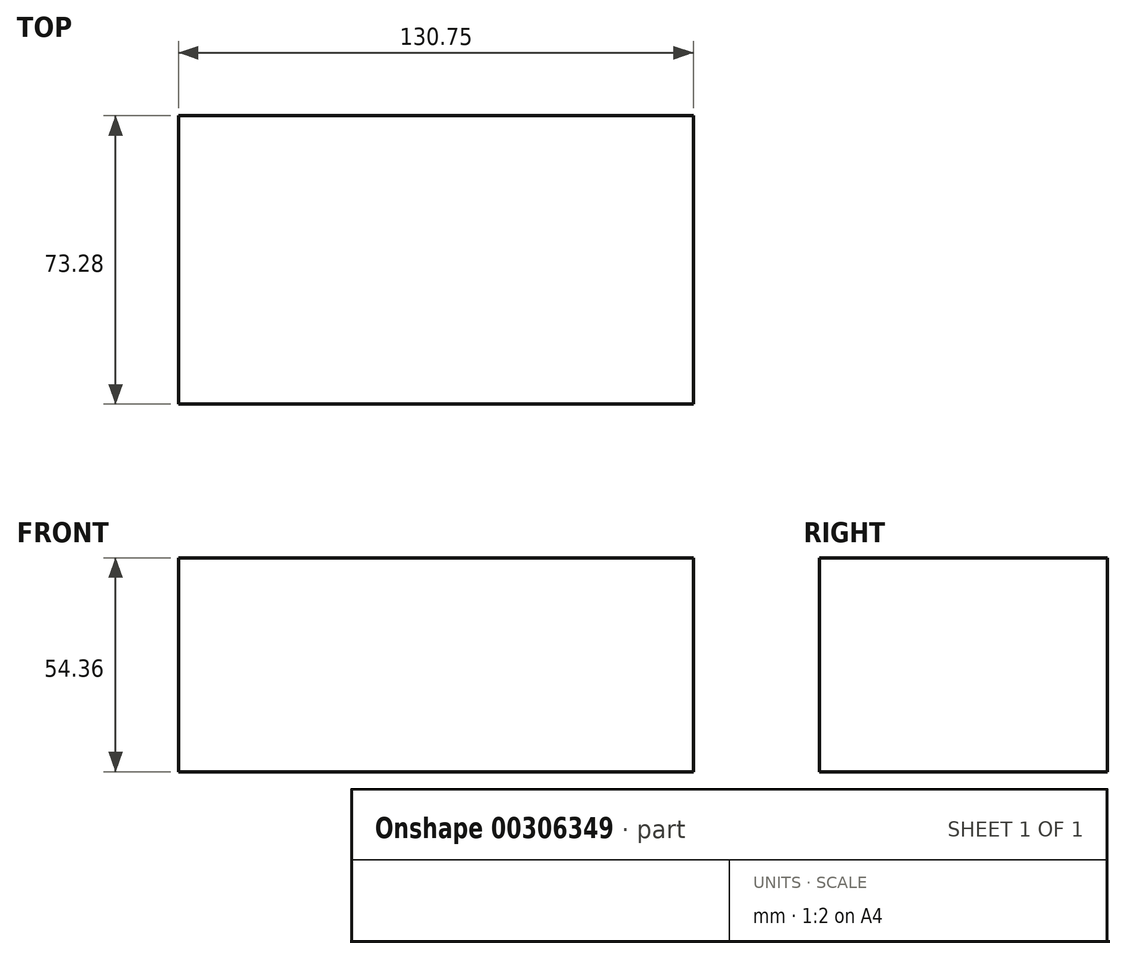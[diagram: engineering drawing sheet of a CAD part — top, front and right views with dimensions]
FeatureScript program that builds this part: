
annotation { "Feature Type Name" : "Feature", "Feature Type Description" : "" }
export const myFeature = defineFeature(function(context is Context, id is Id, definition is map)
    precondition{}
    {
        {
            var Q0;
            Q0=qCreatedBy(makeId("Top.planeOp"),FACE);
            var sketch = newSketch(context, id + "F0", { "sketchPlane" : qUnion([Q0])});
            skLineSegment(sketch, "E0.bottom", {"start": v(-61.48, 0) * mm, "end": v(69.27, 0) * mm});
            skLineSegment(sketch, "E0.top", {"start": v(-61.48, 73.28) * mm, "end": v(69.27, 73.28) * mm});
            skLineSegment(sketch, "E0.left", {"start": v(-61.48, 0) * mm, "end": v(-61.48, 73.28) * mm});
            skLineSegment(sketch, "E0.right", {"start": v(69.27, 0) * mm, "end": v(69.27, 73.28) * mm});
            skSolve(sketch);
        }
        {
            var Q0;
            Q0=makeQuery(id+"F0.imprint","IMPRINT",FACE,{"disambiguationData":[TD([[makeQuery(id+"F0.imprint","IMPRINT",EDGE,{"derivedFrom":sQuery(id+"F0.wireOp",EDGE,"E0.bottom")}),1.0]])]});
            extrude(context, id + "F1", {"entities" : qUnion([Q0]), "depth" : 54.36 * mm});
        }
    });
